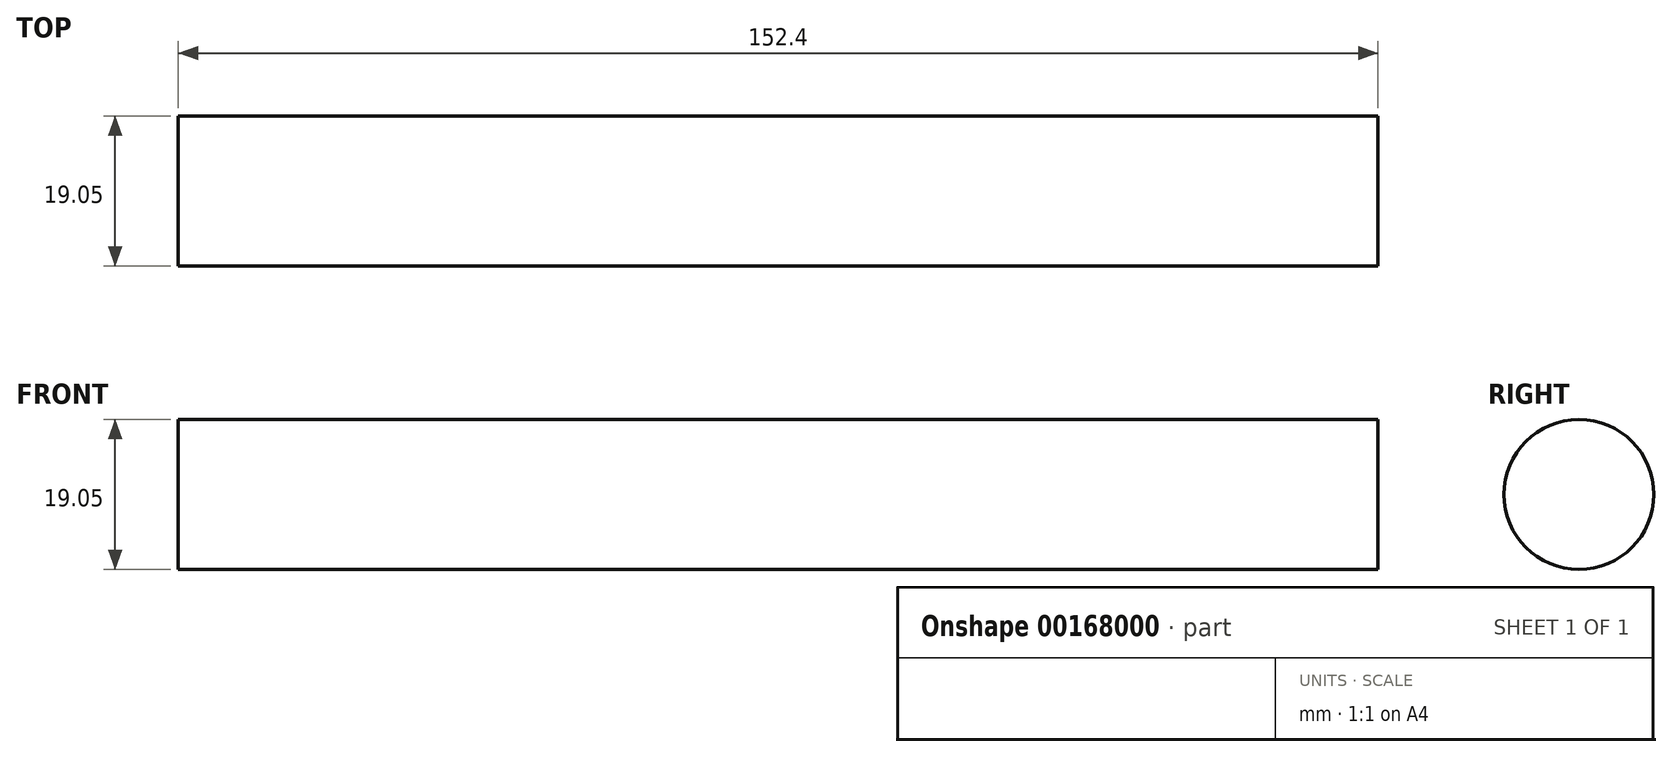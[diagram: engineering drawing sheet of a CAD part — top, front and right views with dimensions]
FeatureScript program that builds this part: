
annotation { "Feature Type Name" : "Feature", "Feature Type Description" : "" }
export const myFeature = defineFeature(function(context is Context, id is Id, definition is map)
    precondition{}
    {
        {
            var Q0;
            Q0=qCreatedBy(makeId("Right.planeOp"),FACE);
            var sketch = newSketch(context, id + "F0", { "sketchPlane" : qUnion([Q0])});
            skCircle(sketch, "E0", {"center": v(-12.44, 17.83) * mm, "radius": 9.53 * mm});
            skSolve(sketch);
        }
        {
            var Q0;
            Q0=makeQuery(id+"F0.imprint","IMPRINT",FACE,{"disambiguationData":[TD([[makeQuery(id+"F0.imprint","IMPRINT",EDGE,{"derivedFrom":sQuery(id+"F0.wireOp",EDGE,"E0")}),1.0]])]});
            extrude(context, id + "F1", {"entities" : qUnion([Q0]), "depth" : 152.4 * mm});
        }
    });
